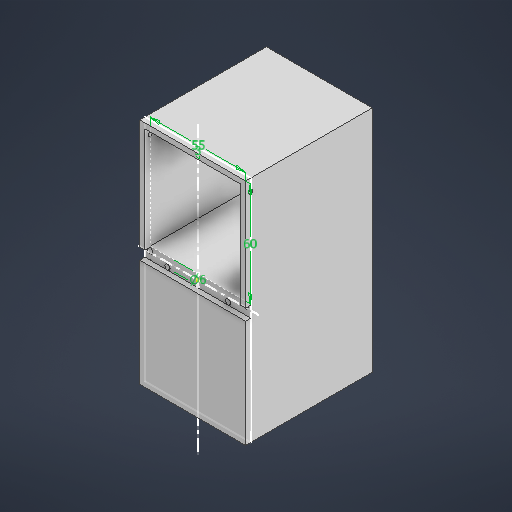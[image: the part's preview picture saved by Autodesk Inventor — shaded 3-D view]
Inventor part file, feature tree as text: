
AUTODESK INVENTOR PART (.ipt)
format: ipt  version: 2025.3 (Build 293356030, 356C)  size: 273,408 bytes
history: native  units: mm
features: extrude x7, sketch x7, other x1, shell x1
ambient origin geometry x8: Origin, YZ Plane, XZ Plane, XY Plane, X Axis, Y Axis, Z Axis, Center Point
bodies: Body1 (feature_tree)
feature tree (16):
  other  "實體1"
  extrude  "擠出1"  Depth=55.0mm
  shell  "薄殼1"  Thickness=60.0mm
  extrude  "擠出2"  Depth=3.0mm
  extrude  "擠出3"  Depth=6.0mm
  extrude  "擠出4"  Depth=3.0mm TaperAngle=0.0deg
  extrude  "擠出5"  Depth=55.0mm
  extrude  "擠出6"  Depth=8.0mm
  extrude  "擠出7"  Depth=3.0mm TaperAngle=0.0deg
  sketch  "草圖1"
  sketch  "草圖2"
  sketch  "草圖3"
  sketch  "草圖4"
  sketch  "草圖5"
  sketch  "草圖6"
  sketch  "草圖7"
